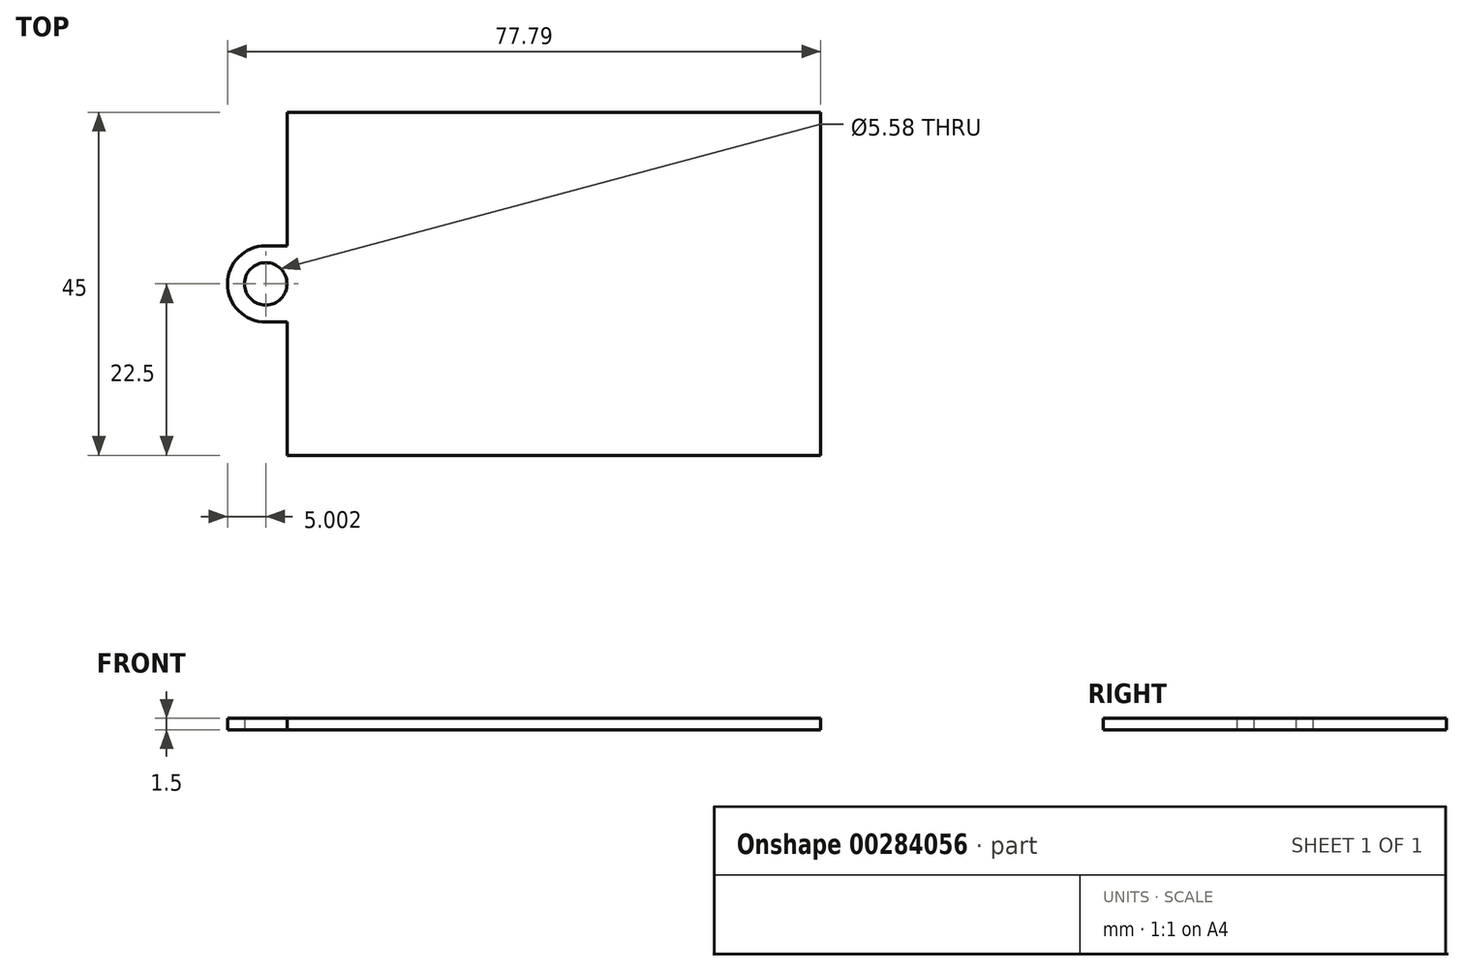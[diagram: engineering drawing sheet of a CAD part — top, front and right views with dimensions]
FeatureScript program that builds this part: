
annotation { "Feature Type Name" : "Feature", "Feature Type Description" : "" }
export const myFeature = defineFeature(function(context is Context, id is Id, definition is map)
    precondition{}
    {
        {
            var Q0;
            Q0=qCreatedBy(makeId("Top.planeOp"),FACE);
            var sketch = newSketch(context, id + "F0", { "sketchPlane" : qUnion([Q0])});
            skLineSegment(sketch, "E0.bottom", {"start": v(-35, 22.5) * mm, "end": v(35, 22.5) * mm});
            skLineSegment(sketch, "E0.top", {"start": v(-35, -22.5) * mm, "end": v(35, -22.5) * mm});
            skLineSegment(sketch, "E0.left", {"start": v(-35, 22.5) * mm, "end": v(-35, 5) * mm});
            skLineSegment(sketch, "E0.right", {"start": v(35, 22.5) * mm, "end": v(35, -22.5) * mm});
            skPoint(sketch, "E0.middle", {"position": v(0, 0) * mm});
            skArc(sketch, "E1", {"start": v(-37.79, 5) * mm, "mid": v(-42.8, 0) * mm, "end": v(-37.79, -5) * mm});
            skLineSegment(sketch, "E2", {"start": v(-37.79, 5) * mm, "end": v(-35, 5) * mm});
            skLineSegment(sketch, "E3", {"start": v(-37.79, -5) * mm, "end": v(-35, -5) * mm});
            skLineSegment(sketch, "E4.trimOffspring", {"start": v(-35, -5) * mm, "end": v(-35, -22.5) * mm});
            skCircle(sketch, "E5", {"center": v(-37.79, 0) * mm, "radius": 2.79 * mm});
            skSolve(sketch);
        }
        {
            var Q0;
            Q0=makeQuery(id+"F0.imprint","IMPRINT",FACE,{"disambiguationData":[TD([[makeQuery(id+"F0.imprint","IMPRINT",EDGE,{"derivedFrom":sQuery(id+"F0.wireOp",EDGE,"E0.bottom")}),-1.0]])]});
            extrude(context, id + "F1", {"entities" : qUnion([Q0]), "depth" : 1.5 * mm});
        }
    });
